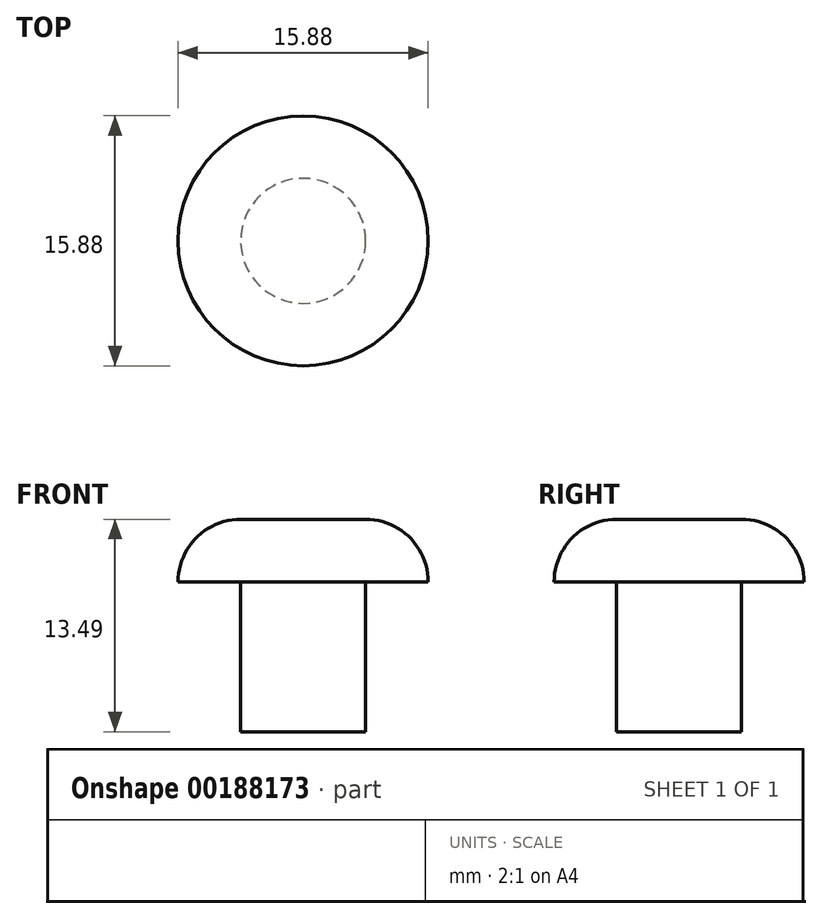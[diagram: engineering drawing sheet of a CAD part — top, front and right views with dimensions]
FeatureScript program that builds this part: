
annotation { "Feature Type Name" : "Feature", "Feature Type Description" : "" }
export const myFeature = defineFeature(function(context is Context, id is Id, definition is map)
    precondition{}
    {
        {
            var Q0;
            Q0=qCreatedBy(makeId("Front.planeOp"),FACE);
            var sketch = newSketch(context, id + "F0", { "sketchPlane" : qUnion([Q0])});
            skLineSegment(sketch, "E0", {"start": v(0, 0) * mm, "end": v(3.97, 0) * mm});
            skLineSegment(sketch, "E1", {"start": v(3.97, 0) * mm, "end": v(3.97, 9.53) * mm});
            skLineSegment(sketch, "E2", {"start": v(3.97, 9.53) * mm, "end": v(7.94, 9.53) * mm});
            skLineSegment(sketch, "E3", {"start": v(0, 0) * mm, "end": v(0, 13.5) * mm});
            skLineSegment(sketch, "E4", {"start": v(0, 13.5) * mm, "end": v(3.97, 13.5) * mm});
            skLineSegment(sketch, "E5", {"start": v(0, 27.15) * mm, "end": v(0, -11.23) * mm, "construction": true});
            skArc(sketch, "E6", {"start": v(7.94, 9.53) * mm, "mid": v(6.78, 12.33) * mm, "end": v(3.97, 13.5) * mm});
            skSolve(sketch);
        }
        {
            var Q0;
            Q0=makeQuery(id+"F0.imprint","IMPRINT",FACE,{"disambiguationData":[TD([[makeQuery(id+"F0.imprint","IMPRINT",EDGE,{"derivedFrom":sQuery(id+"F0.wireOp",EDGE,"E0")}),1.0]])]});
            var Q1;
            Q1=sQuery(id+"F0.wireOp",EDGE,"E5");
            revolve(context, id + "F1", {"entities" : qUnion([Q0]), "axis" : qUnion([Q1]), "revolveType" : RevolveType.FULL});
        }
    });
